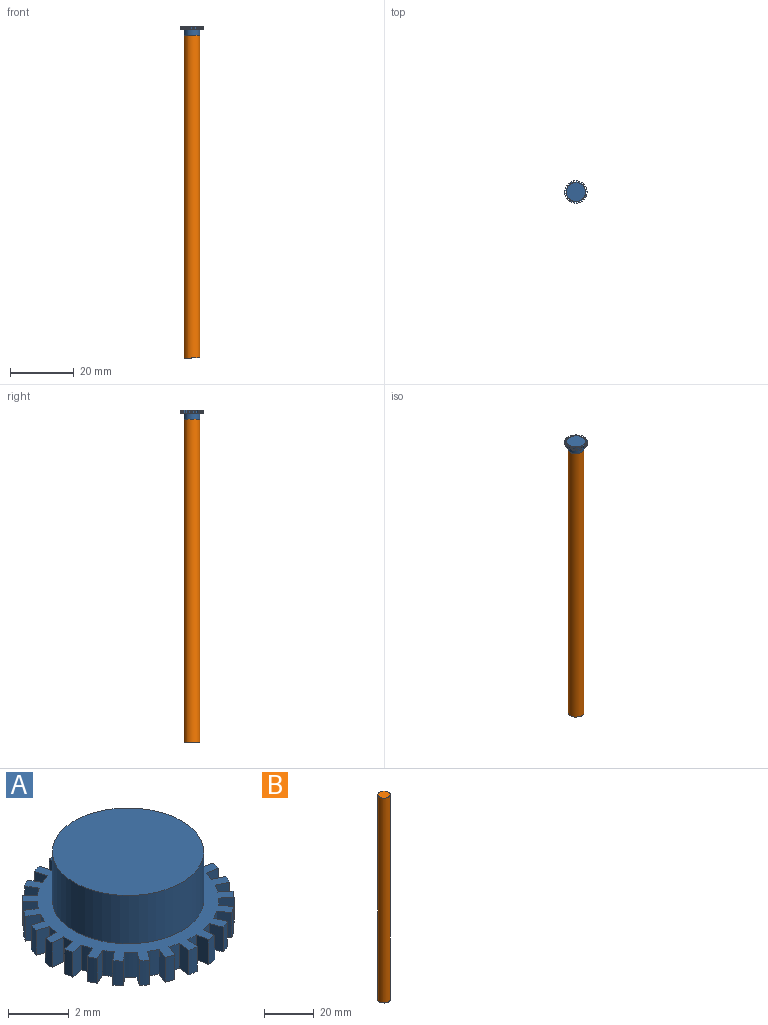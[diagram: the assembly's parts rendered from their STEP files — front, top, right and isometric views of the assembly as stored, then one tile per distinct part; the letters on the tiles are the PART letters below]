
ASSEMBLY  parts=2 mates=1
PART A: 104 faces, bbox 7x7x3 mm
  f0: cylinder r=3.5mm len=1mm, axis (0,0,-1), area 0.4mm2, adj f1,f99,f100,f101
  f1: plane 1x0.5mm, normal (-0.06,-1,0), area 0.5mm2, adj f0,f2,f100,f101
  f2: cylinder r=3mm len=1mm, axis (0,0,-1), area 0.4mm2, adj f1,f3,f100,f101
  f3: plane 1x0.49mm, normal (-0.19,0.98,0), area 0.5mm2, adj f2,f4,f100,f101
  f4: cylinder r=3.5mm len=1mm, axis (0,0,-1), area 0.4mm2, adj f3,f5,f100,f101
  f5: plane 1x0.49mm, normal (0.19,-0.98,0), area 0.5mm2, adj f4,f6,f100,f101
  f6: cylinder r=3mm len=1mm, axis (0,0,-1), area 0.4mm2, adj f5,f7,f100,f101
  f7: plane 1x0.45mm, normal (-0.43,0.9,0), area 0.5mm2, adj f6,f8,f100,f101
  f8: cylinder r=3.5mm len=1mm, axis (0,0,-1), area 0.4mm2, adj f7,f9,f100,f101
  f9: plane 1x0.45mm, normal (0.43,-0.9,0), area 0.5mm2, adj f8,f10,f100,f101
  f10: cylinder r=3mm len=1mm, axis (0,0,-1), area 0.4mm2, adj f9,f11,f100,f101
  f11: plane 1x0.39mm, normal (-0.64,0.77,0), area 0.5mm2, adj f10,f12,f100,f101
  f12: cylinder r=3.5mm len=1mm, axis (0,0,-1), area 0.4mm2, adj f11,f13,f100,f101
  f13: plane 1x0.39mm, normal (0.64,-0.77,0), area 0.5mm2, adj f12,f14,f100,f101
  f14: cylinder r=3mm len=1mm, axis (0,0,-1), area 0.4mm2, adj f13,f15,f100,f101
  f15: plane 1x0.4mm, normal (-0.81,0.59,0), area 0.5mm2, adj f14,f16,f100,f101
  f16: cylinder r=3.5mm len=1mm, axis (0,0,-1), area 0.4mm2, adj f15,f17,f100,f101
  f17: plane 1x0.4mm, normal (0.81,-0.59,0), area 0.5mm2, adj f16,f18,f100,f101
  f18: cylinder r=3mm len=1mm, axis (0,0,-1), area 0.4mm2, adj f17,f19,f100,f101
  f19: plane 1x0.47mm, normal (-0.93,0.37,0), area 0.5mm2, adj f18,f20,f100,f101
  f20: cylinder r=3.5mm len=1mm, axis (0,0,-1), area 0.4mm2, adj f19,f21,f100,f101
  f21: plane 1x0.47mm, normal (0.93,-0.37,0), area 0.5mm2, adj f20,f22,f100,f101
  f22: cylinder r=3mm len=1mm, axis (0,0,-1), area 0.4mm2, adj f21,f23,f100,f101
  f23: plane 1x0.5mm, normal (-0.99,0.13,0), area 0.5mm2, adj f22,f24,f100,f101
  f24: cylinder r=3.5mm len=1mm, axis (0,0,-1), area 0.4mm2, adj f23,f25,f100,f101
  f25: plane 1x0.5mm, normal (0.99,-0.13,0), area 0.5mm2, adj f24,f26,f100,f101
  f26: cylinder r=3mm len=1mm, axis (0,0,-1), area 0.4mm2, adj f25,f27,f100,f101
  f27: plane 1x0.5mm, normal (-0.99,-0.13,0), area 0.5mm2, adj f26,f28,f100,f101
  f28: cylinder r=3.5mm len=1mm, axis (0,0,-1), area 0.4mm2, adj f27,f29,f100,f101
  f29: plane 1x0.5mm, normal (0.99,0.13,0), area 0.5mm2, adj f28,f30,f100,f101
  f30: cylinder r=3mm len=1mm, axis (0,0,-1), area 0.4mm2, adj f29,f31,f100,f101
  f31: plane 1x0.47mm, normal (-0.93,-0.37,0), area 0.5mm2, adj f30,f32,f100,f101
  f32: cylinder r=3.5mm len=1mm, axis (0,0,-1), area 0.4mm2, adj f31,f33,f100,f101
  f33: plane 1x0.47mm, normal (0.93,0.37,0), area 0.5mm2, adj f32,f34,f100,f101
  f34: cylinder r=3mm len=1mm, axis (0,0,-1), area 0.4mm2, adj f33,f35,f100,f101
  f35: plane 1x0.4mm, normal (-0.81,-0.59,0), area 0.5mm2, adj f34,f36,f100,f101
  f36: cylinder r=3.5mm len=1mm, axis (0,0,-1), area 0.4mm2, adj f35,f37,f100,f101
  f37: plane 1x0.4mm, normal (0.81,0.59,0), area 0.5mm2, adj f36,f38,f100,f101
  f38: cylinder r=3mm len=1mm, axis (0,0,-1), area 0.4mm2, adj f37,f39,f100,f101
  f39: plane 1x0.39mm, normal (-0.64,-0.77,0), area 0.5mm2, adj f38,f40,f100,f101
  f40: cylinder r=3.5mm len=1mm, axis (0,0,-1), area 0.4mm2, adj f39,f41,f100,f101
  f41: plane 1x0.39mm, normal (0.64,0.77,0), area 0.5mm2, adj f40,f42,f100,f101
  f42: cylinder r=3mm len=1mm, axis (0,0,-1), area 0.4mm2, adj f41,f43,f100,f101
  f43: plane 1x0.45mm, normal (-0.43,-0.9,0), area 0.5mm2, adj f42,f44,f100,f101
  f44: cylinder r=3.5mm len=1mm, axis (0,0,-1), area 0.4mm2, adj f43,f45,f100,f101
  f45: plane 1x0.45mm, normal (0.43,0.9,0), area 0.5mm2, adj f44,f46,f100,f101
  f46: cylinder r=3mm len=1mm, axis (0,0,-1), area 0.4mm2, adj f45,f47,f100,f101
  f47: plane 1x0.49mm, normal (-0.19,-0.98,0), area 0.5mm2, adj f46,f48,f100,f101
  f48: cylinder r=3.5mm len=1mm, axis (0,0,-1), area 0.4mm2, adj f47,f49,f100,f101
  f49: plane 1x0.49mm, normal (0.19,0.98,0), area 0.5mm2, adj f48,f50,f100,f101
  f50: cylinder r=3mm len=1mm, axis (0,0,-1), area 0.4mm2, adj f49,f51,f100,f101
  f51: plane 1x0.5mm, normal (0.06,-1,0), area 0.5mm2, adj f50,f52,f100,f101
  f52: cylinder r=3.5mm len=1mm, axis (0,0,-1), area 0.4mm2, adj f51,f53,f100,f101
  f53: plane 1x0.5mm, normal (-0.06,1,0), area 0.5mm2, adj f52,f54,f100,f101
  f54: cylinder r=3mm len=1mm, axis (0,0,-1), area 0.4mm2, adj f53,f55,f100,f101
  f55: plane 1x0.48mm, normal (0.31,-0.95,0), area 0.5mm2, adj f54,f56,f100,f101
  f56: cylinder r=3.5mm len=1mm, axis (0,0,-1), area 0.4mm2, adj f55,f57,f100,f101
  f57: plane 1x0.48mm, normal (-0.31,0.95,0), area 0.5mm2, adj f56,f58,f100,f101
  f58: cylinder r=3mm len=1mm, axis (0,0,-1), area 0.4mm2, adj f57,f59,f100,f101
  f59: plane 1x0.42mm, normal (0.54,-0.84,0), area 0.5mm2, adj f58,f60,f100,f101
  f60: cylinder r=3.5mm len=1mm, axis (0,0,-1), area 0.4mm2, adj f59,f61,f100,f101
  f61: plane 1x0.42mm, normal (-0.54,0.84,0), area 0.5mm2, adj f60,f62,f100,f101
  f62: cylinder r=3mm len=1mm, axis (0,0,-1), area 0.4mm2, adj f61,f63,f100,f101
  f63: plane 1x0.36mm, normal (0.73,-0.68,0), area 0.5mm2, adj f62,f64,f100,f101
  f64: cylinder r=3.5mm len=1mm, axis (0,0,-1), area 0.4mm2, adj f63,f65,f100,f101
  f65: plane 1x0.36mm, normal (-0.73,0.68,0), area 0.5mm2, adj f64,f66,f100,f101
  f66: cylinder r=3mm len=1mm, axis (0,0,-1), area 0.4mm2, adj f65,f67,f100,f101
  f67: plane 1x0.44mm, normal (0.88,-0.48,0), area 0.5mm2, adj f66,f68,f100,f101
  f68: cylinder r=3.5mm len=1mm, axis (0,0,-1), area 0.4mm2, adj f67,f69,f100,f101
  f69: plane 1x0.44mm, normal (-0.88,0.48,0), area 0.5mm2, adj f68,f70,f100,f101
  f70: cylinder r=3mm len=1mm, axis (0,0,-1), area 0.4mm2, adj f69,f71,f100,f101
  f71: plane 1x0.48mm, normal (0.97,-0.25,0), area 0.5mm2, adj f70,f72,f100,f101
  f72: cylinder r=3.5mm len=1mm, axis (0,0,-1), area 0.4mm2, adj f71,f73,f100,f101
  f73: plane 1x0.48mm, normal (-0.97,0.25,0), area 0.5mm2, adj f72,f74,f100,f101
  f74: cylinder r=3mm len=1mm, axis (0,0,-1), area 0.4mm2, adj f73,f75,f100,f101
  f75: plane 1x0.5mm, normal (1,0,0), area 0.5mm2, adj f74,f76,f100,f101
  f76: cylinder r=3.5mm len=1mm, axis (0,0,-1), area 0.4mm2, adj f75,f77,f100,f101
  f77: plane 1x0.5mm, normal (-1,0,0), area 0.5mm2, adj f76,f78,f100,f101
  f78: cylinder r=3mm len=1mm, axis (0,0,-1), area 0.4mm2, adj f77,f79,f100,f101
  f79: plane 1x0.48mm, normal (0.97,0.25,0), area 0.5mm2, adj f78,f80,f100,f101
  f80: cylinder r=3.5mm len=1mm, axis (0,0,-1), area 0.4mm2, adj f79,f81,f100,f101
  f81: plane 1x0.48mm, normal (-0.97,-0.25,0), area 0.5mm2, adj f80,f82,f100,f101
  f82: cylinder r=3mm len=1mm, axis (0,0,-1), area 0.4mm2, adj f81,f83,f100,f101
  f83: plane 1x0.44mm, normal (0.88,0.48,0), area 0.5mm2, adj f82,f84,f100,f101
  f84: cylinder r=3.5mm len=1mm, axis (0,0,-1), area 0.4mm2, adj f83,f85,f100,f101
  f85: plane 1x0.44mm, normal (-0.88,-0.48,0), area 0.5mm2, adj f84,f86,f100,f101
  f86: cylinder r=3mm len=1mm, axis (0,0,-1), area 0.4mm2, adj f85,f87,f100,f101
  f87: plane 1x0.36mm, normal (0.73,0.68,0), area 0.5mm2, adj f86,f88,f100,f101
  f88: cylinder r=3.5mm len=1mm, axis (0,0,-1), area 0.4mm2, adj f87,f89,f100,f101
  f89: plane 1x0.36mm, normal (-0.73,-0.68,0), area 0.5mm2, adj f88,f90,f100,f101
  f90: cylinder r=3mm len=1mm, axis (0,0,-1), area 0.4mm2, adj f89,f91,f100,f101
  f91: plane 1x0.42mm, normal (0.54,0.84,0), area 0.5mm2, adj f90,f92,f100,f101
  f92: cylinder r=3.5mm len=1mm, axis (0,0,-1), area 0.4mm2, adj f91,f93,f100,f101
  f93: plane 1x0.42mm, normal (-0.54,-0.84,0), area 0.5mm2, adj f92,f94,f100,f101
  f94: cylinder r=3mm len=1mm, axis (0,0,-1), area 0.4mm2, adj f93,f95,f100,f101
  f95: plane 1x0.48mm, normal (0.31,0.95,0), area 0.5mm2, adj f94,f96,f100,f101
  f96: cylinder r=3.5mm len=1mm, axis (0,0,-1), area 0.4mm2, adj f95,f97,f100,f101
  f97: plane 1x0.48mm, normal (-0.31,-0.95,0), area 0.5mm2, adj f96,f98,f100,f101
  f98: cylinder r=3mm len=1mm, axis (0,0,-1), area 0.4mm2, adj f97,f99,f100,f101
  f99: plane 1x0.5mm, normal (0.06,1,0), area 0.5mm2, adj f0,f98,f100,f101
  f100: plane 7x6.99mm, normal (0,0,1), area 13mm2, adj f0,f1,f2,f3,f4,f5,f6,f7
  f101: plane 7x6.99mm, normal (0,0,-1), area 32.7mm2, adj f0,f1,f2,f3,f4,f5,f6,f7
  f102: cylinder r=2.5mm len=5mm, axis (0,0,-1), area 30.6mm2, adj f100,f103
  f103: plane 5x5mm, normal (0,0,1), area 19.6mm2, adj f102
PART B: 3 faces, bbox 5x5x101 mm
  f0: plane 5x5mm, normal (0,0,1), area 19.6mm2, adj f1
  f1: cylinder r=2.5mm len=101mm, axis (0,0,-1), area 1586.5mm2, adj f0,f2
  f2: plane 5x5mm, normal (0,0,-1), area 19.6mm2, adj f1
PLACE A rot(axis=(-0.98,0.21,0),180deg) t=(-4.89,12.2,103.95)mm
PLACE B rot(axis=(0,0,-1),24.8deg) t=(6.81,-4.2,50)mm
MATE fastened B.f1 <-> A.f0  axis (0,0,1) through (0,-1.06,101)mm
